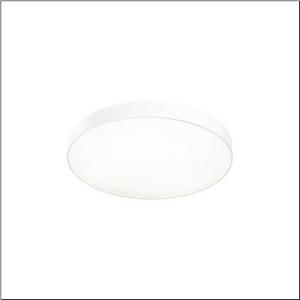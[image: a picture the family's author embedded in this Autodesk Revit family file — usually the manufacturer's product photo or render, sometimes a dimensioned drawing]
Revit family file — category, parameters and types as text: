
# Revit family: round_21_m_51mr36gd0421w
name_source: partatom
category: Lighting Fixtures
units: mm (PartAtom-declared; Revit-internal decimal feet)

## family parameters
Cut with Voids When Loaded = No
Host = Face
Light Source = No
Part Type = Normal
Room Calculation Point = No
Round Connector Dimension = Use Diameter
Shared = No

## types (1)
- Round 21 M (1 x LED, 7870 lm, 54.6 W, 4000K)
    Apparent Load = 55 VA
    CIE Flux Codes = 49 80 96 85 100
    Color Rendering = 80
    Color Temperature = 4000K
    Default Elevation = 1800 mm
    Description = Round 21 M, wall and ceiling luminaire, primary optical cover: cover, of PMMA, opal, light emission: direct/indirect distribution, primary light characteristic: symmetric, installation type: suspended mounting, surface-mounted, LED, rated luminous flux: 7.870lm, luminous efficacy: 144lm/W, light colour: 840, colour temperature: 4000K, control gear: DALI 2, with terminal, 5-pole, mains connection: 230V, AC, 50/60Hz, rated input power: 54.6W, housing, of aluminium, coated, white, diameter: 600mm, height: 62mm, protection rating (complete): IP40, insulation class (complete): insulation class I (protective earthing), certification: CE, impact resistance: IK04, permissible operating ambient temperature: -10..+35°C, packaging unit: 1 piece
    Height = 87 mm
    Lamp = 1 x LED
    Lamp Light Flux = 7870 lm
    Lamp Power = 54.6 W
    Lamp count = 1
    Length = 600 mm
    Luminous efficacy = 144 lm/W
    Manufacturer = Siteco
    ModVariant = No
    Model = 51MR36GD0421W
    Mounting Place = Ceiling
    Mounting Type = Surface mounted
    Number of Poles = 1
    OnlyDefault = Yes
    Power Factor = 1
    Product Name = Round 21 M
    Product group = wall and ceiling luminaire
    ProductGroupID = 304
    Protection Class = Protection class I
    Protection Degree = IP 40
    RLX_Detail_Level = 1
    RLX_Emergency_Light_Flux = 0 lm
    RLX_Emergency_Type = 0
    RLX_Emergency_Type_DB = No
    RlxData = <blob elided: 12129 chars, md5=08d00f86>
    Socket = socket
    Standby Power = 0 W
    System Light Flux = 7870 lm
    System Power = 55 W
    Type Comments = Product without accessories
    Type Image = l_1258330.jpg
    URL = http://relux.com
    VarID = ---
    Voltage = 0 V
    Weight = 0.00 kg
    Width = 0 mm  [stored 0 ft]

note: [stored X ft] marks values corroborated as IEEE doubles in the binary element streams (Revit-internal decimal feet)

## geometry (parser evidence)
native form markers: Sweep x11
no freeform markers — native parametric forms only
